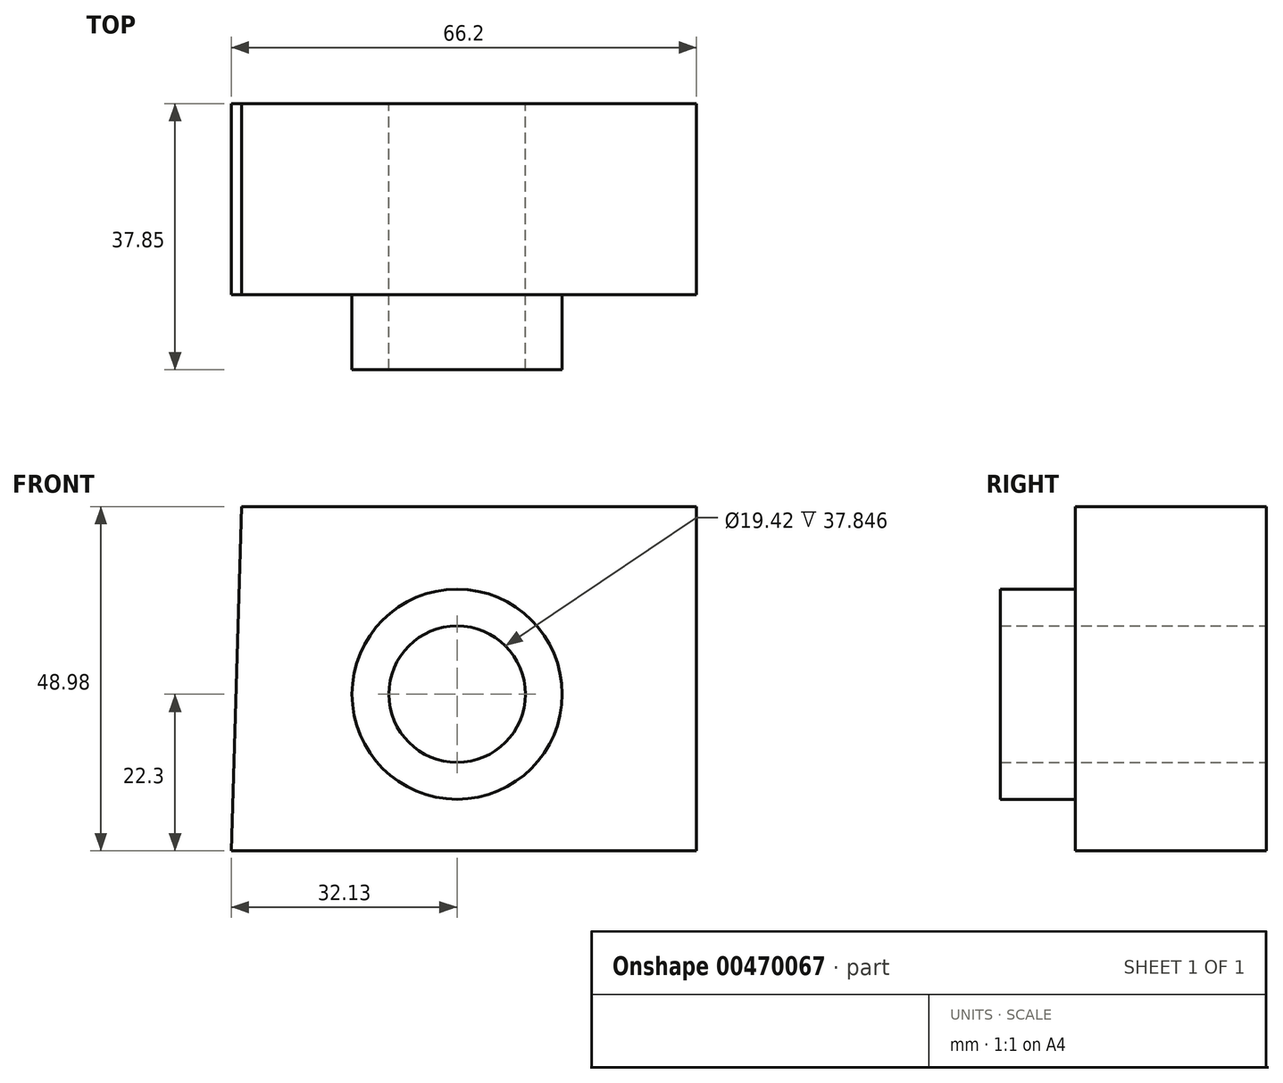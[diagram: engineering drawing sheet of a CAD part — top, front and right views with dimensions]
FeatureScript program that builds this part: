
annotation { "Feature Type Name" : "Feature", "Feature Type Description" : "" }
export const myFeature = defineFeature(function(context is Context, id is Id, definition is map)
    precondition{}
    {
        {
            var Q0;
            Q0=qCreatedBy(makeId("Front.planeOp"),FACE);
            var sketch = newSketch(context, id + "F0", { "sketchPlane" : qUnion([Q0])});
            skLineSegment(sketch, "E0", {"start": v(-30.67, 26.68) * mm, "end": v(34.07, 26.68) * mm});
            skLineSegment(sketch, "E1", {"start": v(34.07, 26.68) * mm, "end": v(34.07, -22.3) * mm});
            skLineSegment(sketch, "E2", {"start": v(34.07, -22.3) * mm, "end": v(-32.13, -22.3) * mm});
            skLineSegment(sketch, "E3", {"start": v(-32.13, -22.3) * mm, "end": v(-30.67, 26.68) * mm});
            skCircle(sketch, "E4", {"center": v(0, 0) * mm, "radius": 9.7 * mm});
            skSolve(sketch);
        }
        {
            var Q0;
            Q0 = qSketchRegion(id + "F0", true);
            extrude(context, id + "F1", {"entities" : qUnion([Q0]), "depth" : 27.18 * mm});
        }
        {
            var Q0;
            Q0=makeQuery(id+"F1.opExtrude","CAP_FACE",FACE,{"disambiguationData":[OSD([sQuery(id+"F0.wireOp",EDGE,"E0"),sQuery(id+"F0.wireOp",EDGE,"E1"),sQuery(id+"F0.wireOp",EDGE,"E2"),sQuery(id+"F0.wireOp",EDGE,"E3"),sQuery(id+"F0.wireOp",EDGE,"E4")])],"isStart":false});
            var sketch = newSketch(context, id + "F2", { "sketchPlane" : qUnion([Q0])});
            skCircle(sketch, "E5", {"center": v(0, 0) * mm, "radius": 14.95 * mm});
            skSolve(sketch);
        }
        {
            var Q0;
            Q0=makeQuery(id+"F2.imprint","IMPRINT",FACE,{"disambiguationData":[TD([[makeQuery(id+"F2.imprint","IMPRINT",EDGE,{"derivedFrom":sQuery(id+"F2.wireOp",EDGE,"E5")}),1.0]])]});
            extrude(context, id + "F3", {"entities" : qUnion([Q0]), "operationType" : NewBodyOperationType.ADD, "depth" : 10.67 * mm});
        }
    });
